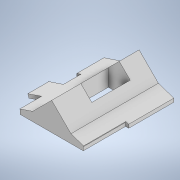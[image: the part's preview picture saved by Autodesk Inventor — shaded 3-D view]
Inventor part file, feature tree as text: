
AUTODESK INVENTOR PART (.ipt)
format: ipt  version: 2022.1 (Build 261234000, 234)  size: 184,832 bytes
history: native  units: in
note: dims shown in document units (in); Inventor stores cm internally (conversion verified against a paired STEP export)
features: extrude x7, sketch x7, plane x1
ambient origin geometry x8: Origin, YZ Plane, XZ Plane, XY Plane, X Axis, Y Axis, Z Axis, Center Point
bodies: Solid1 (feature_tree)
feature tree (15):
  extrude  "Extrusion1"  Depth=116.5in
  extrude  "Extrusion2"  Depth=185.0in
  extrude  "Extrusion3"  Depth=187.0in
  extrude  "Extrusion4"  Depth=112.0279in
  extrude  "Extrusion5"  Depth=310.0in
  extrude  "Extrusion6"  TaperAngle=0.0deg  [1 undecoded]
  plane  "Work Plane1"
  extrude  "Extrusion7"  Depth=149.0in
  sketch  "Sketch1"  dims[d1=0.1267in d2=116.5in]
  sketch  "Sketch2"  dims[d4=45.0deg d6=185.0in]
  sketch  "Sketch3"  dims[d7=45.0deg d8=187.0in]
  sketch  "Sketch4"  dims[d9=0.1267in d10=112.0279in]
  sketch  "Sketch5"  dims[d11=600.0in d12=0.0in d13=310.0in]
  sketch  "Sketch6"  dims[d14=91.5in d15=0.0in d16=0.0in]
  sketch  "Sketch7"  dims[d17=92.0in d18=149.0in d19=0.0in d20=0.0in d22=187.0in d23=86.0in d24=144.0in d25=0.0in d26=0.0in d27=24.0in d28=0.0in d29=75.0in d30=24.0in d31=0.0in d32=200.0in d33=264.0in d34=150.0in d35=0.0in d36=0.0in]
note: 1 required parameter value undecoded (feature->parameter linkage not recoverable at this tier; creation-order binding heuristic only, values carry confidence <= 0.55)
